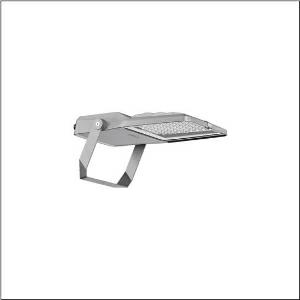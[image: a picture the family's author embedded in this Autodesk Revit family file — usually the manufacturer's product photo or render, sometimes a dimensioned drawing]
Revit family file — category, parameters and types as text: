
# Revit family: floodlight_fl_21_iq_mini___pl33t_5xa7772b4f1a_67af
name_source: partatom
category: Lighting Fixtures
units: mm (PartAtom-declared; Revit-internal decimal feet)

## family parameters
Cut with Voids When Loaded = No
Host = Face
Light Source = No
Part Type = Normal
Room Calculation Point = No
Round Connector Dimension = Use Diameter
Shared = No

## types (1)
- --- (1 x LED, 6420 lm, 45.5 W, 4000K)
    Apparent Load = 46 VA
    CIE Flux Codes = 26 75 99 100 100
    Color Rendering = 70
    Color Temperature = 4000K
    Default Elevation = 1800 mm
    Description = Floodlight FL 21 iQ mini, floodlight, primary light control with lens, of PMMA, primary optical cover: protective disc, of toughened safety glass, transparent, light distribution: PL33T, light emission: direct distribution, installation type: surface-mounted, lamps: LED, High Power LED, rated values: 6.420lm | 45,5W | 141,1lm/W (begin service life); end service life: 6.420lm | 48W; at 50% lumin. flux: 3.210lm | 21,5W | 149,3lm/W, colour temperature: 4000K, colour rendering: CRI > 70, light colour: 740, light setting 1 begin service life: 100% | 6.420lm | 45,5W | 141,1lm/W | 4.000K, light setting 1 end service life: 48W, further light settings possible, control: Street-Remote, Auto-Match, Temp-Guard, Night-Set, Smart-Wire, Desk-Remote (wireless, voltage-free reading and setting of iQ features in the workshop via application-optimized NFC function/RFID function), optimised constant luminous flux control (CLO 2.0), pre-setting: linear dimming characteristic, with terminal, 6-pole, mains connection: 220..240V, AC, 50/60Hz, luminaire housing, of diecast aluminium, powder-coated, SITECO metallic grey (DB 702S), corrosivity category C5 mid according to DIN EN ISO 12944suitable for swimming poolschlorine-resistant, sealing non-destructively replaceable, mounting bracket, of steel, galvanised, powder-coated, SITECO metallic grey (DB 702S), protection rating (complete): IP66, insulation class (complete): insulation class II (safety insulation), certification: CE, ENEC, VDE, protection symbol: D, impact resistance: IK08, permissible operating ambient temperature: -40..+40°C, permissible operating ambient temperature for outdoor applications: -40..+50°C, standard: DIN EN 12944, LABS conformity tested according to VDMA 24364:2018-05, packaging unit: 1 piece

Light Distribution: PL33T
    Height = 70 mm
    Lamp = 1 x LED
    Lamp Light Flux = 6420 lm
    Lamp Power = 45.5 W
    Lamp count = 1
    Length = 485 mm
    Luminous efficacy = 141 lm/W
    Manufacturer = Siteco
    ModVariant = No
    Model = 5XA7772B4F1A
    Number of Poles = 1
    OnlyDefault = Yes
    Power Factor = 1
    Product Name = Floodlight FL 21 iQ mini | PL33T
    Product group = floodlight | pylon annexe
    ProductGroupID = 6201
    Protection Class = Protection class II
    Protection Degree = IP 66
    RLX_Detail_Level = 1
    RLX_Emergency_Light_Flux = 0 lm
    RLX_Emergency_Type = 0
    RLX_Emergency_Type_DB = No
    RlxData = <blob elided: 96377 chars, md5=47846251>
    Socket = socket
    Standby Power = 0 W
    System Light Flux = 6420 lm
    System Power = 46 W
    Type Comments = factory setting: luminous flux: 100 % | dim-lin: 254 | 463 mA
    Type Image = l_1006845.jpg
    URL = http://relux.com
    VarID = @adj_149455
    Voltage = 0 V
    Weight = 0.00 kg
    Width = 337 mm

## geometry (parser evidence)
native form markers: Blend x4, Sweep x11
no freeform markers — native parametric forms only
